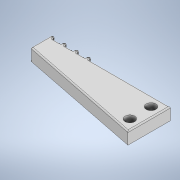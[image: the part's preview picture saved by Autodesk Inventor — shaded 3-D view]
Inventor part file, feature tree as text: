
AUTODESK INVENTOR PART (.ipt)
format: ipt  version: 2021 (Build 250183000, 183)  size: 207,360 bytes
history: native  units: mm
features: extrude x2, sketch x2, fillet x1
ambient origin geometry x8: Origin, YZ Plane, XZ Plane, XY Plane, X Axis, Y Axis, Z Axis, Center Point
bodies: Solid1 (feature_tree)
feature tree (5):
  extrude  "Extrusion1"  Depth=5.8mm
  extrude  "Extrusion2"  Depth=0.33mm
  fillet  "Fillet1"  Radius=0.84mm
  sketch  "Sketch1"  dims[d0=11.66mm d1=5.8mm]
  sketch  "Sketch2"  dims[d2=33.33mm d3=5.0mm d4=0.84mm d5=0.84mm d6=40.0mm d8=3.33mm d9=10.0mm d11=10.0mm d13=3.33mm d14=0.0mm d15=2.66mm d16=2.664mm d17=5.8mm d18=2.66mm d19=2.66mm d20=10.0mm d21=0.0mm d22=0.33mm]
